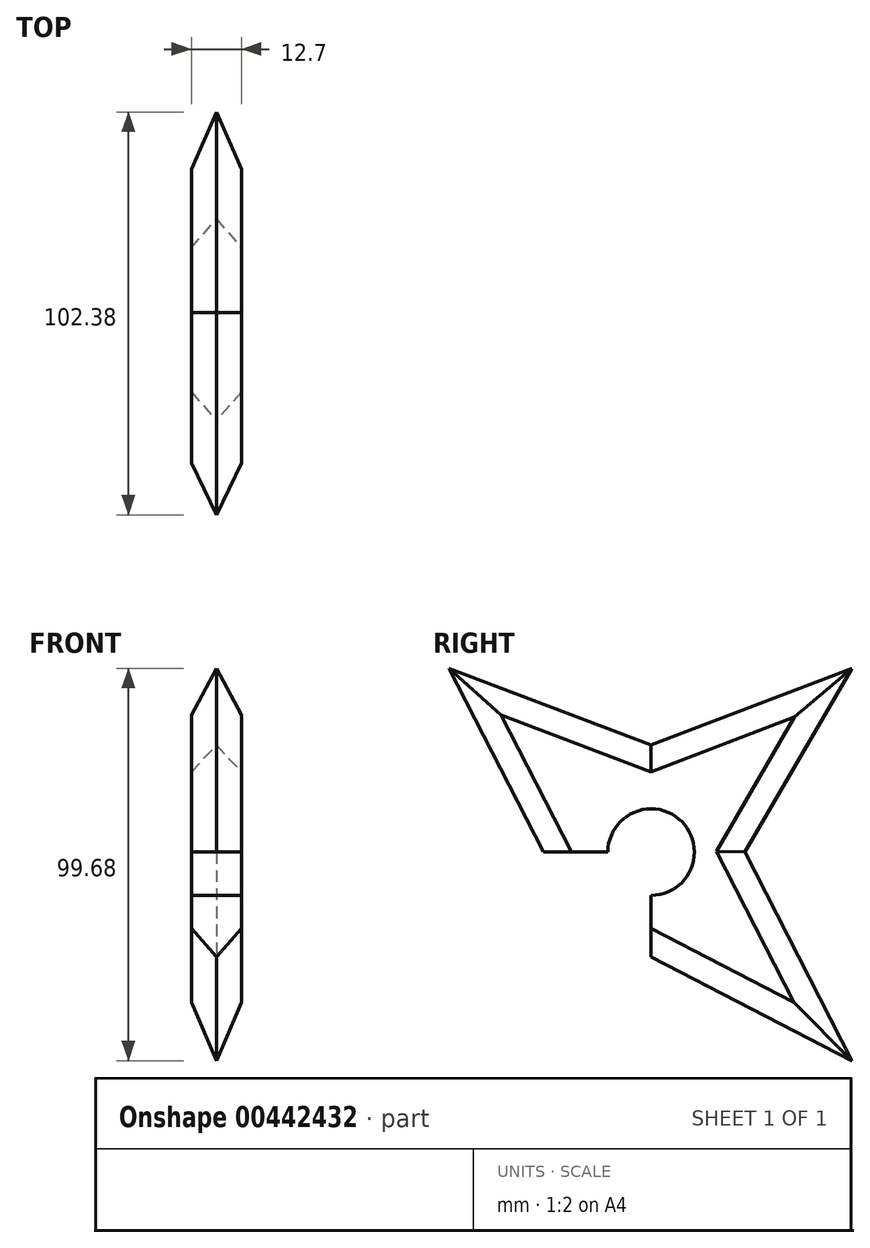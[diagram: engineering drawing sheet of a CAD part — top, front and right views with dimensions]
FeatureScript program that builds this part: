
annotation { "Feature Type Name" : "Feature", "Feature Type Description" : "" }
export const myFeature = defineFeature(function(context is Context, id is Id, definition is map)
    precondition{}
    {
        {
            var Q0;
            Q0=qCreatedBy(makeId("Right.planeOp"),FACE);
            var sketch = newSketch(context, id + "F0", { "sketchPlane" : qUnion([Q0])});
            skLineSegment(sketch, "E0", {"start": v(-51.34, 46.69) * mm, "end": v(-27.32, 0) * mm});
            skLineSegment(sketch, "E1", {"start": v(-27.32, 0) * mm, "end": v(0, 0) * mm});
            skLineSegment(sketch, "E2", {"start": v(0, 0) * mm, "end": v(0, 27.17) * mm});
            skLineSegment(sketch, "E3", {"start": v(0, 27.17) * mm, "end": v(-51.34, 46.69) * mm});
            skLineSegment(sketch, "E4", {"start": v(0, 0) * mm, "end": v(-27.32, 0) * mm});
            skLineSegment(sketch, "E5", {"start": v(-27.32, 0) * mm, "end": v(-51.34, -52.99) * mm});
            skLineSegment(sketch, "E6", {"start": v(-51.34, -52.99) * mm, "end": v(0, -26.58) * mm});
            skLineSegment(sketch, "E7", {"start": v(0, -26.58) * mm, "end": v(0, 0) * mm});
            skLineSegment(sketch, "E8", {"start": v(0, -26.58) * mm, "end": v(51.04, -52.99) * mm});
            skLineSegment(sketch, "E9", {"start": v(51.04, -52.99) * mm, "end": v(23.78, 0) * mm});
            skLineSegment(sketch, "E10", {"start": v(23.78, 0) * mm, "end": v(0, 0) * mm});
            skLineSegment(sketch, "E11", {"start": v(23.78, 0) * mm, "end": v(51.04, 46.69) * mm});
            skLineSegment(sketch, "E12", {"start": v(51.04, 46.69) * mm, "end": v(0, 27.17) * mm});
            skSolve(sketch);
        }
        {
            var Q0;
            Q0=makeQuery(id+"F0.imprint","IMPRINT",FACE,{"disambiguationData":[TD([[makeQuery(id+"F0.imprint","IMPRINT",EDGE,{"derivedFrom":sQuery(id+"F0.wireOp",EDGE,"E0")}),1.0]])]});
            var Q1;
            Q1=makeQuery(id+"F0.imprint","IMPRINT",FACE,{"disambiguationData":[TD([[makeQuery(id+"F0.imprint","IMPRINT",EDGE,{"derivedFrom":sQuery(id+"F0.wireOp",EDGE,"E4")}),1.0]])]});
            var Q2;
            Q2=makeQuery(id+"F0.imprint","IMPRINT",FACE,{"disambiguationData":[TD([[makeQuery(id+"F0.imprint","IMPRINT",EDGE,{"derivedFrom":sQuery(id+"F0.wireOp",EDGE,"E7")}),-1.0]])]});
            var Q3;
            Q3=makeQuery(id+"F0.imprint","IMPRINT",FACE,{"disambiguationData":[TD([[makeQuery(id+"F0.imprint","IMPRINT",EDGE,{"derivedFrom":sQuery(id+"F0.wireOp",EDGE,"E2")}),-1.0]])]});
            extrude(context, id + "F1", {"entities" : qUnion([Q0, Q1, Q2, Q3]), "depth" : 12.7 * mm});
        }
        {
            var Q0;
            Q0=makeQuery(id+"F1.opExtrude","CAP_EDGE",EDGE,{"disambiguationData":[OSD([sQuery(id+"F0.wireOp",EDGE,"E0")])],"isStart":false});
            var Q1;
            Q1=makeQuery(id+"F1.opExtrude","CAP_EDGE",EDGE,{"disambiguationData":[OSD([sQuery(id+"F0.wireOp",EDGE,"E0")])],"isStart":true});
            var Q2;
            Q2=makeQuery(id+"F1.opExtrude","CAP_EDGE",EDGE,{"disambiguationData":[OSD([sQuery(id+"F0.wireOp",EDGE,"E3")])],"isStart":true});
            var Q3;
            Q3=makeQuery(id+"F1.opExtrude","CAP_EDGE",EDGE,{"disambiguationData":[OSD([sQuery(id+"F0.wireOp",EDGE,"E3")])],"isStart":false});
            var Q4;
            Q4=makeQuery(id+"F1.opExtrude","CAP_EDGE",EDGE,{"disambiguationData":[OSD([sQuery(id+"F0.wireOp",EDGE,"E5")])],"isStart":true});
            var Q5;
            Q5=makeQuery(id+"F1.opExtrude","CAP_EDGE",EDGE,{"disambiguationData":[OSD([sQuery(id+"F0.wireOp",EDGE,"E6")])],"isStart":true});
            var Q6;
            Q6=makeQuery(id+"F1.opExtrude","CAP_EDGE",EDGE,{"disambiguationData":[OSD([sQuery(id+"F0.wireOp",EDGE,"E6")])],"isStart":false});
            var Q7;
            Q7=makeQuery(id+"F1.opExtrude","CAP_EDGE",EDGE,{"disambiguationData":[OSD([sQuery(id+"F0.wireOp",EDGE,"E5")])],"isStart":false});
            var Q8;
            Q8=makeQuery(id+"F1.opExtrude","CAP_EDGE",EDGE,{"disambiguationData":[OSD([sQuery(id+"F0.wireOp",EDGE,"E8")])],"isStart":true});
            var Q9;
            Q9=makeQuery(id+"F1.opExtrude","CAP_EDGE",EDGE,{"disambiguationData":[OSD([sQuery(id+"F0.wireOp",EDGE,"E8")])],"isStart":false});
            var Q10;
            Q10=makeQuery(id+"F1.opExtrude","CAP_EDGE",EDGE,{"disambiguationData":[OSD([sQuery(id+"F0.wireOp",EDGE,"E9")])],"isStart":true});
            var Q11;
            Q11=makeQuery(id+"F1.opExtrude","CAP_EDGE",EDGE,{"disambiguationData":[OSD([sQuery(id+"F0.wireOp",EDGE,"E9")])],"isStart":false});
            var Q12;
            Q12=makeQuery(id+"F1.opExtrude","CAP_EDGE",EDGE,{"disambiguationData":[OSD([sQuery(id+"F0.wireOp",EDGE,"E11")])],"isStart":true});
            var Q13;
            Q13=makeQuery(id+"F1.opExtrude","CAP_EDGE",EDGE,{"disambiguationData":[OSD([sQuery(id+"F0.wireOp",EDGE,"E11")])],"isStart":false});
            var Q14;
            Q14=makeQuery(id+"F1.opExtrude","CAP_EDGE",EDGE,{"disambiguationData":[OSD([sQuery(id+"F0.wireOp",EDGE,"E12")])],"isStart":true});
            var Q15;
            Q15=makeQuery(id+"F1.opExtrude","CAP_EDGE",EDGE,{"disambiguationData":[OSD([sQuery(id+"F0.wireOp",EDGE,"E12")])],"isStart":false});
            chamfer(context, id + "F2", {"entities" : qUnion([Q0, Q1, Q2, Q3, Q4, Q5, Q6, Q7, Q8, Q9, Q10, Q11, Q12, Q13, Q14, Q15]), "width" : 6.35 * mm, "tangentPropagation" : true});
        }
        {
            var Q0;
            Q0=qCreatedBy(makeId("Right.planeOp"),FACE);
            var sketch = newSketch(context, id + "F3", { "sketchPlane" : qUnion([Q0])});
            skPoint(sketch, "E13", {"position": v(0, 0) * mm});
            skSolve(sketch);
        }
        {
            var Q0;
            Q0=sQuery(id+"F3.wireOp",VERTEX,"E13");
            var Q1;
            Q1=makeQuery(id+"F1.opExtrude","SWEPT_BODY",BODY,{"disambiguationData":[OSD([sQuery(id+"F0.wireOp",EDGE,"E0"),sQuery(id+"F0.wireOp",EDGE,"E3"),sQuery(id+"F0.wireOp",EDGE,"E5"),sQuery(id+"F0.wireOp",EDGE,"E6"),sQuery(id+"F0.wireOp",EDGE,"E8"),sQuery(id+"F0.wireOp",EDGE,"E9"),sQuery(id+"F0.wireOp",EDGE,"E11"),sQuery(id+"F0.wireOp",EDGE,"E12")])]});
            hole(context, id + "F4", {"style" : HoleStyle.SIMPLE, "endStyle" : HoleEndStyle.THROUGH, "oppositeDirection" : true, "standardTappedOrClearance" : lookupTablePath({ "standard" : "ISO", "fit" : "Normal", "size" : "M20", "type" : "Clearance" }), "standardBlindInLast" : lookupTablePath({ "fit" : "Standard", "standard" : "ISO", "size" : "M20", "type" : "Clearance" }), "holeDiameter" : 22 * mm, "isTappedThrough" : true, "tappedDepth" : 12.7 * mm, "tapClearance" : 3, "locations" : qUnion([Q0]), "scope" : qUnion([Q1])});
        }
    });
